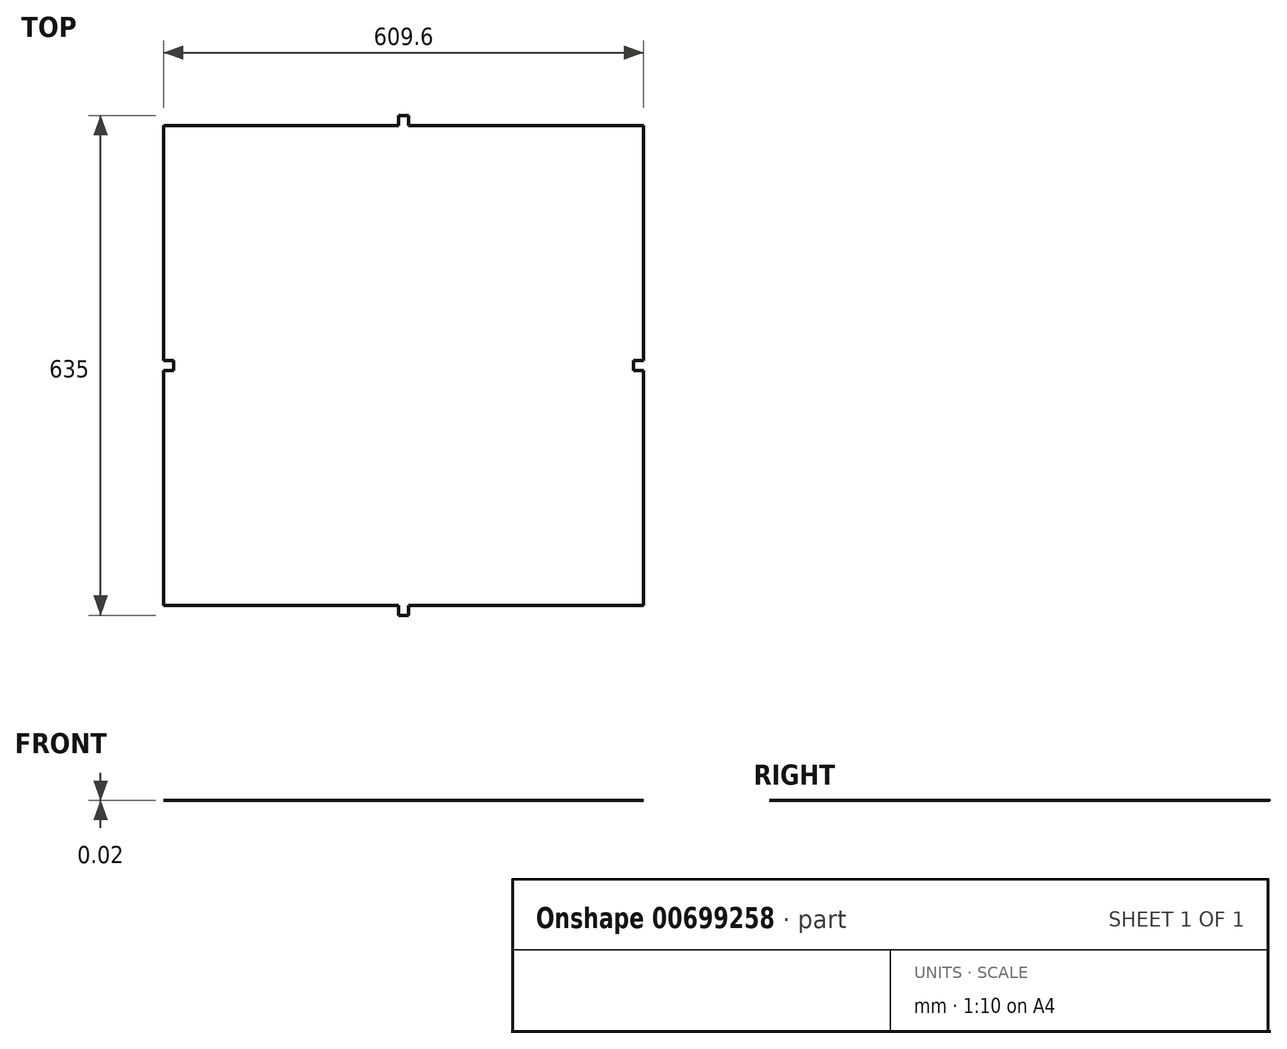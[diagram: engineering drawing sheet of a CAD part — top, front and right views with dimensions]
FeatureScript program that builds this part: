
annotation { "Feature Type Name" : "Feature", "Feature Type Description" : "" }
export const myFeature = defineFeature(function(context is Context, id is Id, definition is map)
    precondition{}
    {
        {
            var Q0;
            Q0=qCreatedBy(makeId("Top.planeOp"),FACE);
            var sketch = newSketch(context, id + "F0", { "sketchPlane" : qUnion([Q0])});
            skLineSegment(sketch, "E0.bottom", {"start": v(304.8, -304.8) * mm, "end": v(-304.8, -304.8) * mm});
            skLineSegment(sketch, "E0.top", {"start": v(304.8, 304.8) * mm, "end": v(-304.8, 304.8) * mm});
            skLineSegment(sketch, "E0.left", {"start": v(304.8, -304.8) * mm, "end": v(304.8, 304.8) * mm});
            skLineSegment(sketch, "E0.right", {"start": v(-304.8, -304.8) * mm, "end": v(-304.8, 304.8) * mm});
            skPoint(sketch, "E0.middle", {"position": v(0, 0) * mm});
            skSolve(sketch);
        }
        {
            var Q0;
            Q0=makeQuery(id+"F0.imprint","IMPRINT",FACE,{"disambiguationData":[TD([[makeQuery(id+"F0.imprint","IMPRINT",EDGE,{"derivedFrom":sQuery(id+"F0.wireOp",EDGE,"E0.bottom")}),-1.0]])]});
            extrude(context, id + "F1", {"entities" : qUnion([Q0]), "endBound" : BoundingType.SYMMETRIC, "oppositeDirection" : true, "depth" : 5 / 203.2 * mm, "offsetDistance" : 25.4 * mm});
        }
        {
            var Q0;
            Q0=makeQuery(id+"F1.opExtrude","SWEPT_FACE",FACE,{"disambiguationData":[OSD([sQuery(id+"F0.wireOp",EDGE,"E0.left")])]});
            var sketch = newSketch(context, id + "F2", { "sketchPlane" : qUnion([Q0])});
            skCircle(sketch, "E1", {"center": v(0, 0) * mm, "radius": 6.35 * mm});
            skSolve(sketch);
        }
        {
            var Q0;
            Q0=makeQuery(id+"F2.imprint","IMPRINT",FACE,{"disambiguationData":[TD([[makeQuery(id+"F2.imprint","IMPRINT",EDGE,{"derivedFrom":sQuery(id+"F2.wireOp",EDGE,"E1")}),1.0]])]});
            extrude(context, id + "F3", {"entities" : qUnion([Q0]), "operationType" : NewBodyOperationType.REMOVE, "oppositeDirection" : true, "depth" : 12.7 * mm, "offsetDistance" : 25.4 * mm});
        }
        {
            var Q0;
            Q0=makeQuery(id+"F1.opExtrude","SWEPT_FACE",FACE,{"disambiguationData":[OSD([sQuery(id+"F0.wireOp",EDGE,"E0.bottom")])]});
            var sketch = newSketch(context, id + "F4", { "sketchPlane" : qUnion([Q0])});
            skCircle(sketch, "E2", {"center": v(0, 0) * mm, "radius": 6.35 * mm});
            skSolve(sketch);
        }
        {
            var Q0;
            Q0=makeQuery(id+"F4.imprint","IMPRINT",FACE,{"disambiguationData":[TD([[makeQuery(id+"F4.imprint","IMPRINT",EDGE,{"derivedFrom":sQuery(id+"F4.wireOp",EDGE,"E2")}),1.0]])]});
            extrude(context, id + "F5", {"entities" : qUnion([Q0]), "operationType" : NewBodyOperationType.ADD, "depth" : 12.7 * mm, "offsetDistance" : 25.4 * mm});
        }
        {
            var Q0;
            Q0=makeQuery(id+"F1.opExtrude","SWEPT_FACE",FACE,{"disambiguationData":[OSD([sQuery(id+"F0.wireOp",EDGE,"E0.right")])]});
            var sketch = newSketch(context, id + "F6", { "sketchPlane" : qUnion([Q0])});
            skCircle(sketch, "E3", {"center": v(0, 0) * mm, "radius": 6.35 * mm});
            skSolve(sketch);
        }
        {
            var Q0;
            Q0=makeQuery(id+"F6.imprint","IMPRINT",FACE,{"disambiguationData":[TD([[makeQuery(id+"F6.imprint","IMPRINT",EDGE,{"derivedFrom":sQuery(id+"F6.wireOp",EDGE,"E3")}),1.0]])]});
            extrude(context, id + "F7", {"entities" : qUnion([Q0]), "operationType" : NewBodyOperationType.REMOVE, "oppositeDirection" : true, "depth" : 12.7 * mm, "offsetDistance" : 25.4 * mm});
        }
        {
            var Q0;
            Q0=makeQuery(id+"F1.opExtrude","SWEPT_FACE",FACE,{"disambiguationData":[OSD([sQuery(id+"F0.wireOp",EDGE,"E0.top")])]});
            var sketch = newSketch(context, id + "F8", { "sketchPlane" : qUnion([Q0])});
            skCircle(sketch, "E4", {"center": v(0, 0) * mm, "radius": 6.35 * mm});
            skSolve(sketch);
        }
        {
            var Q0;
            Q0=makeQuery(id+"F8.imprint","IMPRINT",FACE,{"disambiguationData":[TD([[makeQuery(id+"F8.imprint","IMPRINT",EDGE,{"derivedFrom":sQuery(id+"F8.wireOp",EDGE,"E4")}),1.0]])]});
            extrude(context, id + "F9", {"entities" : qUnion([Q0]), "operationType" : NewBodyOperationType.ADD, "depth" : 12.7 * mm, "offsetDistance" : 25.4 * mm});
        }
    });
